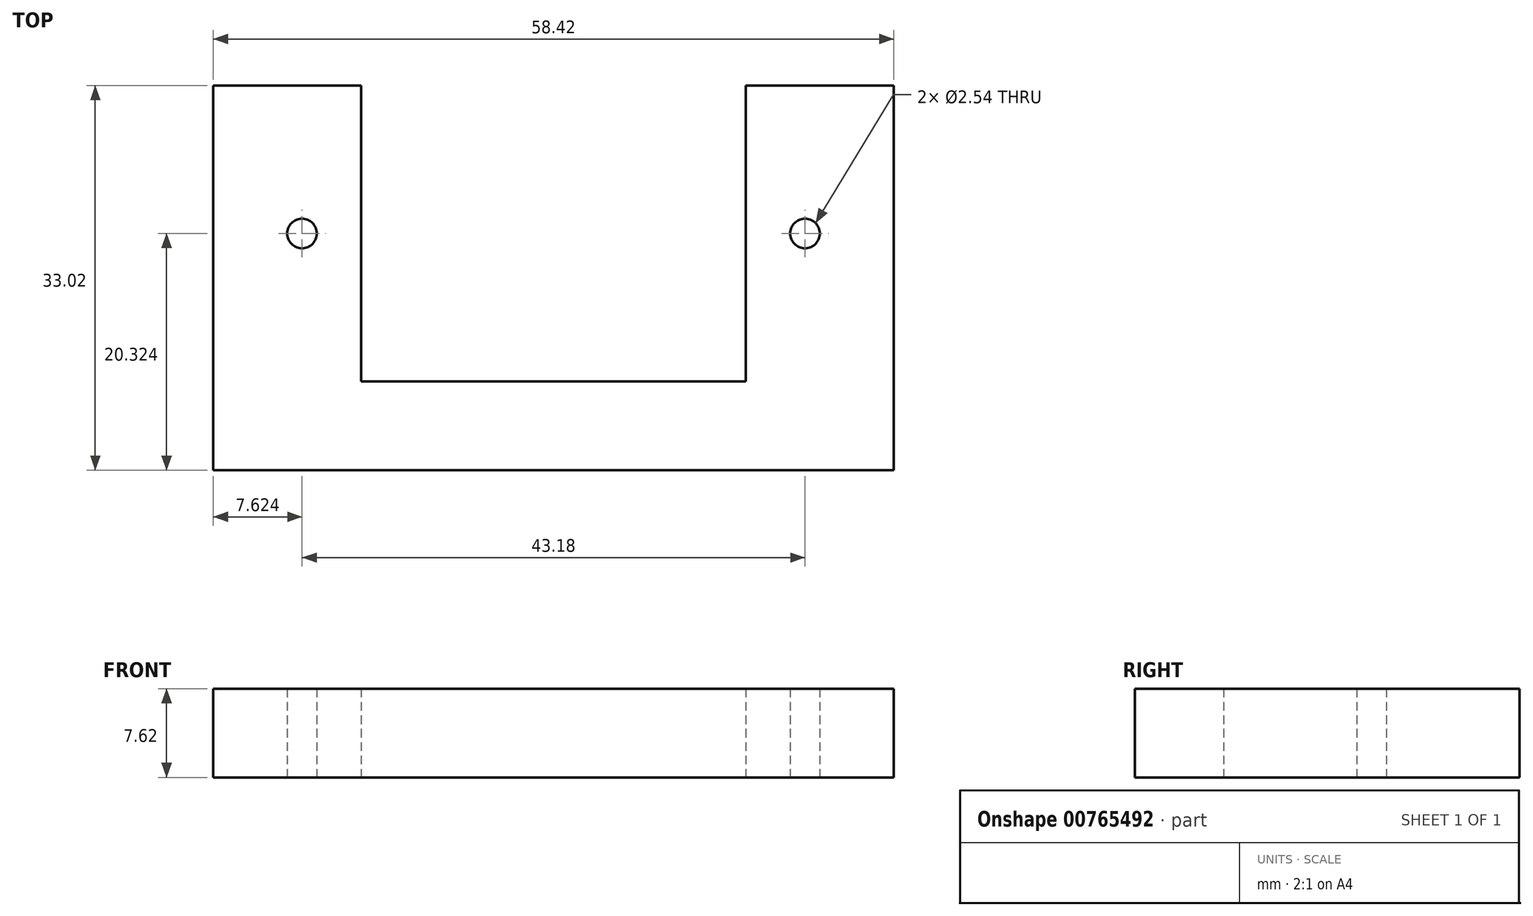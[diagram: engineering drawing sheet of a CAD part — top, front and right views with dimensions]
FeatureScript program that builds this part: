
annotation { "Feature Type Name" : "Feature", "Feature Type Description" : "" }
export const myFeature = defineFeature(function(context is Context, id is Id, definition is map)
    precondition{}
    {
        {
            var Q0;
            Q0=qCreatedBy(makeId("Top.planeOp"),FACE);
            var sketch = newSketch(context, id + "F0", { "sketchPlane" : qUnion([Q0])});
            skLineSegment(sketch, "E0", {"start": v(17.67, 35.54) * mm, "end": v(30.37, 35.54) * mm});
            skLineSegment(sketch, "E1", {"start": v(30.37, 35.54) * mm, "end": v(30.37, 2.52) * mm});
            skLineSegment(sketch, "E2", {"start": v(30.37, 2.52) * mm, "end": v(-28.05, 2.52) * mm});
            skLineSegment(sketch, "E3", {"start": v(-28.05, 2.52) * mm, "end": v(-28.05, 35.54) * mm});
            skLineSegment(sketch, "E4", {"start": v(-28.05, 35.54) * mm, "end": v(-15.35, 35.54) * mm});
            skLineSegment(sketch, "E5", {"start": v(-15.35, 35.54) * mm, "end": v(-15.35, 10.14) * mm});
            skLineSegment(sketch, "E6", {"start": v(-15.35, 10.14) * mm, "end": v(17.67, 10.14) * mm});
            skLineSegment(sketch, "E7", {"start": v(17.67, 10.14) * mm, "end": v(17.67, 35.54) * mm});
            skPoint(sketch, "E8.centerSnap0", {"position": v(-15.35, 22.84) * mm});
            skPoint(sketch, "E9.centerSnap0", {"position": v(17.67, 22.84) * mm});
            skCircle(sketch, "E10", {"center": v(-20.43, 22.84) * mm, "radius": 1.27 * mm});
            skCircle(sketch, "E11", {"center": v(22.75, 22.84) * mm, "radius": 1.27 * mm});
            skSolve(sketch);
        }
        {
            var Q0;
            Q0 = qSketchRegion(id + "F0", true);
            extrude(context, id + "F1", {"entities" : qUnion([Q0]), "depth" : 7.62 * mm, "offsetDistance" : 25.4 * mm});
        }
    });
